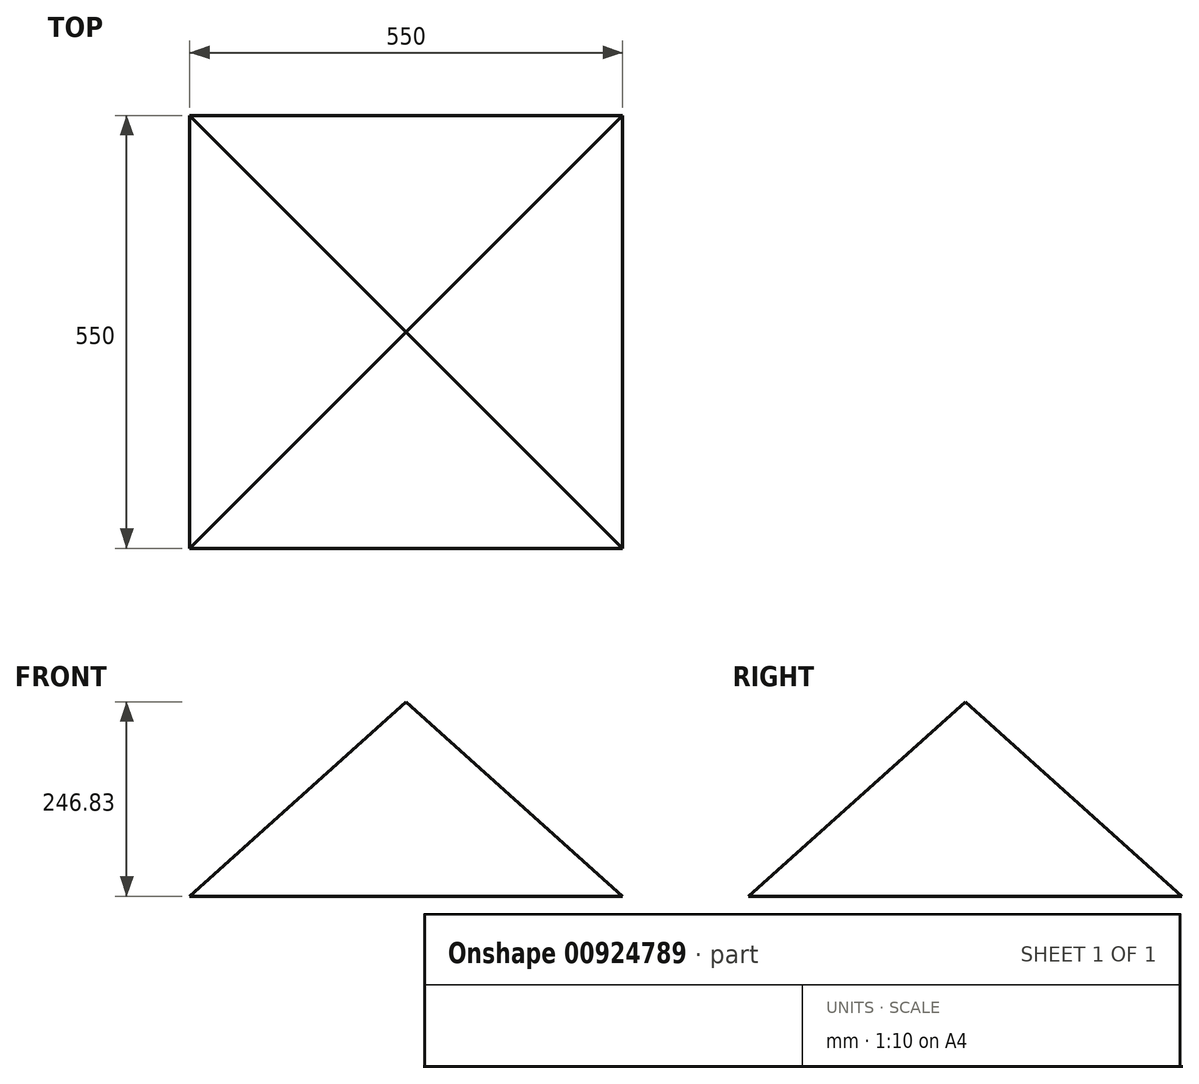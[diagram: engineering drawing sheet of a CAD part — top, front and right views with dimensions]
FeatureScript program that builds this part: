
annotation { "Feature Type Name" : "Feature", "Feature Type Description" : "" }
export const myFeature = defineFeature(function(context is Context, id is Id, definition is map)
    precondition{}
    {
        {
            var Q0;
            Q0=qCreatedBy(makeId("Top.planeOp"),FACE);
            var sketch = newSketch(context, id + "F0", { "sketchPlane" : qUnion([Q0])});
            skLineSegment(sketch, "E0.bottom", {"start": v(-275, -275) * mm, "end": v(275, -275) * mm});
            skLineSegment(sketch, "E0.top", {"start": v(-275, 275) * mm, "end": v(275, 275) * mm});
            skLineSegment(sketch, "E0.left", {"start": v(-275, -275) * mm, "end": v(-275, 275) * mm});
            skLineSegment(sketch, "E0.right", {"start": v(275, -275) * mm, "end": v(275, 275) * mm});
            skSolve(sketch);
        }
        {
            var Q0;
            Q0=makeQuery(id+"F0.imprint","IMPRINT",FACE,{"disambiguationData":[TD([[makeQuery(id+"F0.imprint","IMPRINT",EDGE,{"derivedFrom":sQuery(id+"F0.wireOp",EDGE,"E0.bottom")}),1.0]])]});
            extrude(context, id + "F1", {"entities" : qUnion([Q0]), "depth" : 246.83 * mm, "offsetDistance" : 25 * mm});
        }
        {
            var Q0;
            Q0=makeQuery(id+"F1.opExtrude","CAP_EDGE",EDGE,{"disambiguationData":[OSD([sQuery(id+"F0.wireOp",EDGE,"E0.bottom")])],"isStart":false});
            var Q1;
            Q1=makeQuery(id+"F1.opExtrude","CAP_EDGE",EDGE,{"disambiguationData":[OSD([sQuery(id+"F0.wireOp",EDGE,"E0.top")])],"isStart":false});
            chamfer(context, id + "F2", {"entities" : qUnion([Q0, Q1]), "chamferType" : ChamferType.TWO_OFFSETS, "width1" : 275 * mm, "oppositeDirection" : false, "width2" : 246.83 * mm, "tangentPropagation" : true});
        }
        {
            var Q0;
            Q0=qCreatedBy(makeId("Front.planeOp"),FACE);
            var sketch = newSketch(context, id + "F3", { "sketchPlane" : qUnion([Q0])});
            skLineSegment(sketch, "E1", {"start": v(-275, 0) * mm, "end": v(0, 246.83) * mm});
            skLineSegment(sketch, "E2", {"start": v(0, 246.83) * mm, "end": v(-275, 246.83) * mm});
            skLineSegment(sketch, "E3", {"start": v(-275, 246.83) * mm, "end": v(-275, 0) * mm});
            skLineSegment(sketch, "E4", {"start": v(0, 246.83) * mm, "end": v(0, 109.2) * mm});
            skLineSegment(sketch, "E5.MirrorCS", {"start": v(0, 246.83) * mm, "end": v(275, 246.83) * mm});
            skLineSegment(sketch, "E6.MirrorCS", {"start": v(275, 0) * mm, "end": v(0, 246.83) * mm});
            skLineSegment(sketch, "E7.MirrorCS", {"start": v(275, 246.83) * mm, "end": v(275, 0) * mm});
            skSolve(sketch);
        }
        {
            var Q0;
            Q0 = qSketchRegion(id + "F3", true);
            extrude(context, id + "F4", {"entities" : qUnion([Q0]), "operationType" : NewBodyOperationType.REMOVE, "endBound" : BoundingType.SYMMETRIC, "oppositeDirection" : true, "depth" : 550 * mm, "offsetDistance" : 25 * mm});
        }
    });
